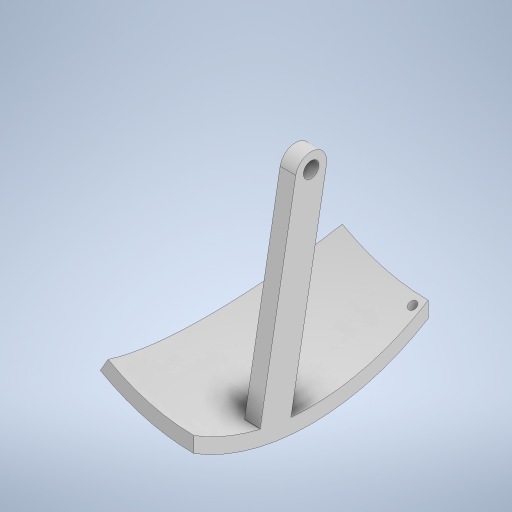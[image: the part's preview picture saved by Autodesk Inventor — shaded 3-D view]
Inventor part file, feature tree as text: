
AUTODESK INVENTOR PART (.ipt)
format: ipt  version: 2023 (Build 270158000, 158)  size: 301,056 bytes
history: native  units: mm
features: sketch x5, hole x3, other x1, revolve x1, extrude x1
ambient origin geometry x8: Origin, YZ Plane, XZ Plane, XY Plane, X Axis, Y Axis, Z Axis, Center Point
bodies: Body1 (feature_tree)
feature tree (11):
  other  "ソリッド1"
  revolve  "回転1"
  extrude  "押し出し1"  Depth=150.0mm
  hole  "穴1"  [1 undecoded]
  hole  "穴3"  [1 undecoded]
  hole  "穴4"  [1 undecoded]
  sketch  "スケッチ1"
  sketch  "スケッチ2"
  sketch  "スケッチ3"
  sketch  "スケッチ5"
  sketch  "スケッチ6"
note: 3 required parameter values undecoded (feature->parameter linkage not recoverable at this tier; creation-order binding heuristic only, values carry confidence <= 0.55)
